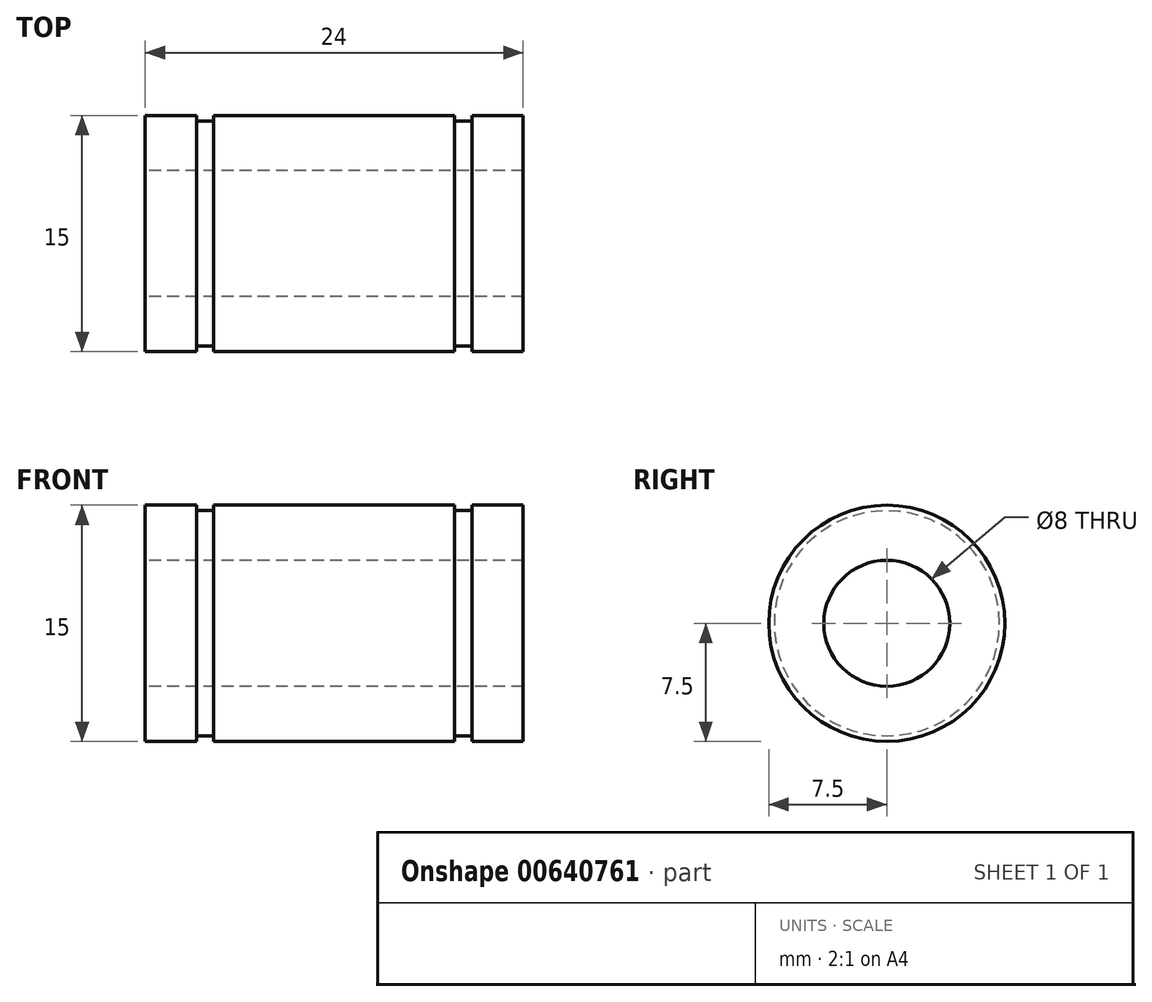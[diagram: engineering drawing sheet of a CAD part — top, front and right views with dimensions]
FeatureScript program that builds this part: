
annotation { "Feature Type Name" : "Feature", "Feature Type Description" : "" }
export const myFeature = defineFeature(function(context is Context, id is Id, definition is map)
    precondition{}
    {
        {
            var Q0;
            Q0=qCreatedBy(makeId("Top.planeOp"),FACE);
            var sketch = newSketch(context, id + "F0", { "sketchPlane" : qUnion([Q0])});
            skLineSegment(sketch, "E0.bottom", {"start": v(-12, 7.5) * mm, "end": v(-6.6, 7.5) * mm});
            skLineSegment(sketch, "E0.top", {"start": v(-12, -7.5) * mm, "end": v(-6.6, -7.5) * mm});
            skLineSegment(sketch, "E0.left", {"start": v(-12, 7.5) * mm, "end": v(-12, 4) * mm});
            skLineSegment(sketch, "E0.right", {"start": v(12, 7.5) * mm, "end": v(12, 4) * mm});
            skPoint(sketch, "E0.middle", {"position": v(0, 0) * mm});
            skLineSegment(sketch, "E1", {"start": v(-12, 4) * mm, "end": v(-12, -4) * mm, "construction": true});
            skLineSegment(sketch, "E2", {"start": v(-12, -4) * mm, "end": v(-12, -7.5) * mm});
            skLineSegment(sketch, "E3", {"start": v(-12, 4) * mm, "end": v(12, 4) * mm});
            skLineSegment(sketch, "E4", {"start": v(-12, -4) * mm, "end": v(12, -4) * mm});
            skLineSegment(sketch, "E5", {"start": v(12, 4) * mm, "end": v(12, -4) * mm, "construction": true});
            skLineSegment(sketch, "E6", {"start": v(12, -4) * mm, "end": v(12, -7.5) * mm});
            skLineSegment(sketch, "E7", {"start": v(-6.6, 7.5) * mm, "end": v(-5.5, 7.5) * mm, "construction": true});
            skLineSegment(sketch, "E8", {"start": v(-5.5, 7.5) * mm, "end": v(9.8, 7.5) * mm});
            skLineSegment(sketch, "E9", {"start": v(9.8, 7.5) * mm, "end": v(10.9, 7.5) * mm, "construction": true});
            skLineSegment(sketch, "E10", {"start": v(10.9, 7.5) * mm, "end": v(12, 7.5) * mm});
            skLineSegment(sketch, "E11", {"start": v(9.8, -7.5) * mm, "end": v(10.9, -7.5) * mm});
            skLineSegment(sketch, "E12", {"start": v(-5.5, -7.5) * mm, "end": v(9.8, -7.5) * mm});
            skLineSegment(sketch, "E13", {"start": v(-6.6, -7.5) * mm, "end": v(-5.5, -7.5) * mm});
            skLineSegment(sketch, "E14", {"start": v(10.9, -7.5) * mm, "end": v(12, -7.5) * mm});
            skLineSegment(sketch, "E15", {"start": v(-6.6, 7.5) * mm, "end": v(-6.6, -7.5) * mm, "construction": true});
            skLineSegment(sketch, "E16", {"start": v(-5.5, 7.5) * mm, "end": v(-5.5, -7.5) * mm, "construction": true});
            skLineSegment(sketch, "E17", {"start": v(9.8, 7.5) * mm, "end": v(9.8, -7.5) * mm, "construction": true});
            skLineSegment(sketch, "E18", {"start": v(10.9, 7.5) * mm, "end": v(10.9, -7.5) * mm, "construction": true});
            skLineSegment(sketch, "E19", {"start": v(-6.6, 7.5) * mm, "end": v(-6.6, 6.7) * mm, "construction": true});
            skLineSegment(sketch, "E20", {"start": v(-6.6, 6.7) * mm, "end": v(-5.5, 6.7) * mm, "construction": true});
            skSolve(sketch);
        }
        {
            var Q0;
            Q0=qCreatedBy(makeId("Top.planeOp"),FACE);
            var sketch = newSketch(context, id + "F1", { "sketchPlane" : qUnion([Q0])});
            skLineSegment(sketch, "E21", {"start": v(-12, 7.5) * mm, "end": v(-8.75, 7.5) * mm});
            skLineSegment(sketch, "E22", {"start": v(-8.75, 7.5) * mm, "end": v(-8.75, 7.15) * mm});
            skLineSegment(sketch, "E23", {"start": v(-8.75, 7.15) * mm, "end": v(-7.65, 7.15) * mm});
            skLineSegment(sketch, "E24", {"start": v(-7.65, 7.15) * mm, "end": v(-7.65, 7.5) * mm});
            skLineSegment(sketch, "E25", {"start": v(-7.65, 7.5) * mm, "end": v(7.65, 7.5) * mm});
            skLineSegment(sketch, "E26", {"start": v(7.65, 7.5) * mm, "end": v(7.65, 7.15) * mm});
            skLineSegment(sketch, "E27", {"start": v(7.65, 7.15) * mm, "end": v(8.75, 7.15) * mm});
            skLineSegment(sketch, "E28", {"start": v(8.75, 7.15) * mm, "end": v(8.75, 7.5) * mm});
            skLineSegment(sketch, "E29", {"start": v(8.75, 7.5) * mm, "end": v(12, 7.5) * mm});
            skLineSegment(sketch, "E30", {"start": v(12, 7.5) * mm, "end": v(12, 4) * mm});
            skLineSegment(sketch, "E31", {"start": v(12, 4) * mm, "end": v(-12, 4) * mm});
            skLineSegment(sketch, "E32", {"start": v(-12, 7.5) * mm, "end": v(-12, 4) * mm});
            skLineSegment(sketch, "E33", {"start": v(8.75, 7.5) * mm, "end": v(7.65, 7.5) * mm, "construction": true});
            skLineSegment(sketch, "E34", {"start": v(-7.65, 7.5) * mm, "end": v(-8.75, 7.5) * mm, "construction": true});
            skLineSegment(sketch, "E35", {"start": v(-7.65, 7.15) * mm, "end": v(7.65, 7.15) * mm, "construction": true});
            skLineSegment(sketch, "E36", {"start": v(0, 0) * mm, "end": v(0, 0) * mm});
            skLineSegment(sketch, "E37", {"start": v(0, 0) * mm, "end": v(12, 0) * mm, "construction": true});
            skSolve(sketch);
        }
        {
            var Q0;
            Q0=makeQuery(id+"F1.imprint","IMPRINT",FACE,{"disambiguationData":[TD([[makeQuery(id+"F1.imprint","IMPRINT",EDGE,{"derivedFrom":sQuery(id+"F1.wireOp",EDGE,"E21")}),-1.0]])]});
            var Q1;
            Q1=sQuery(id+"F1.wireOp",EDGE,"E37");
            revolve(context, id + "F2", {"entities" : qUnion([Q0]), "axis" : qUnion([Q1]), "revolveType" : RevolveType.FULL});
        }
    });
